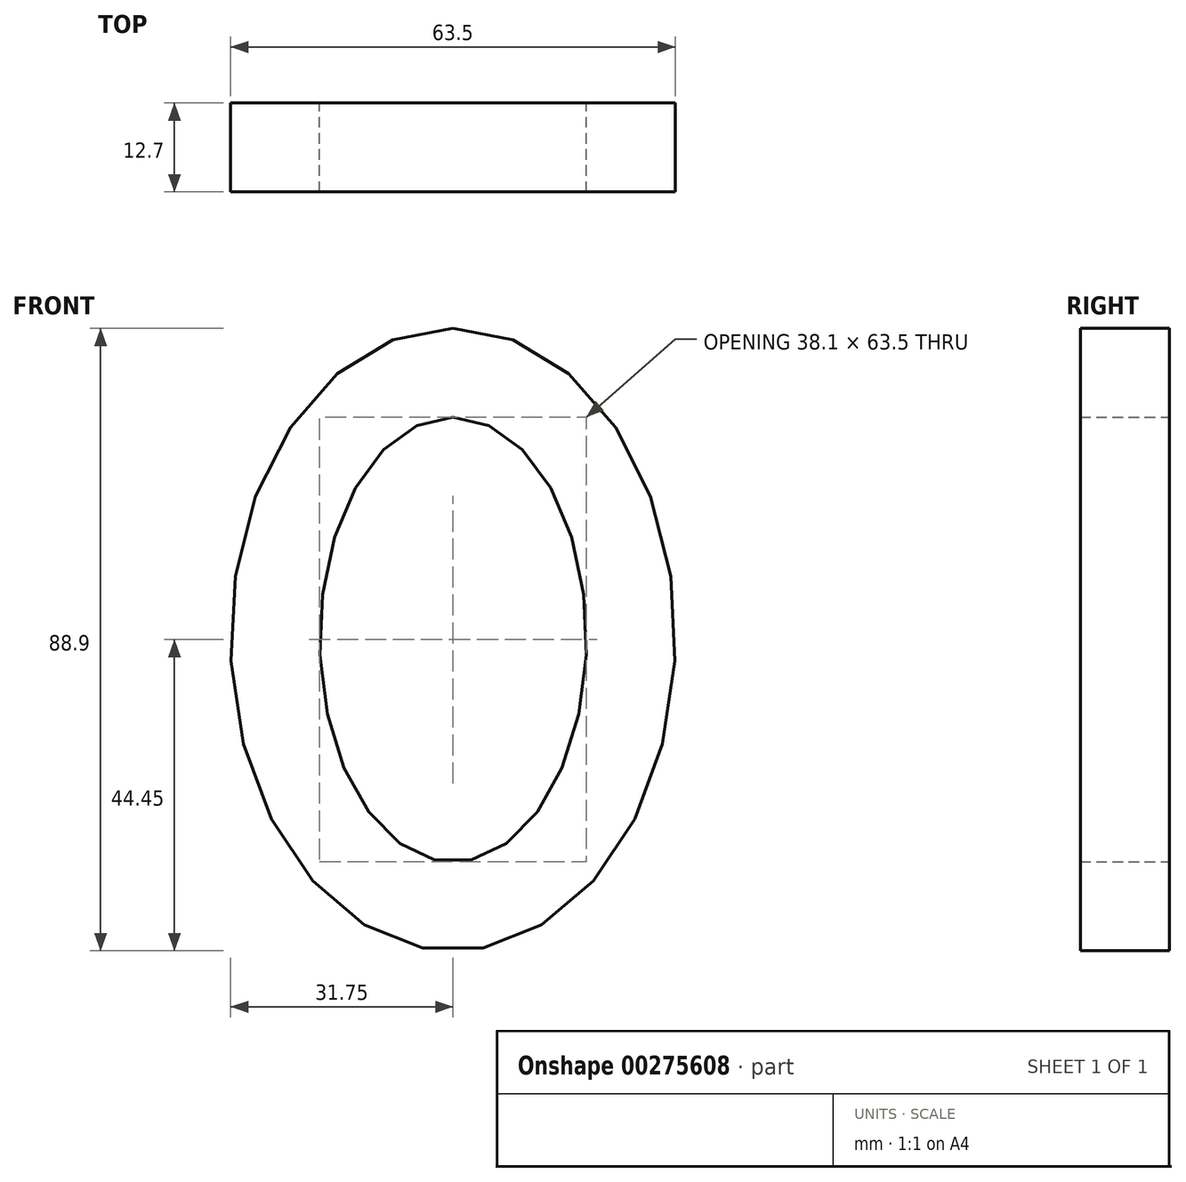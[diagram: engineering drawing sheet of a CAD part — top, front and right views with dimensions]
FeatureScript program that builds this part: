
annotation { "Feature Type Name" : "Feature", "Feature Type Description" : "" }
export const myFeature = defineFeature(function(context is Context, id is Id, definition is map)
    precondition{}
    {
        {
            var Q0;
            Q0=qCreatedBy(makeId("Front.planeOp"),FACE);
            var sketch = newSketch(context, id + "F0", { "sketchPlane" : qUnion([Q0])});
            skEllipse(sketch, "E0", {"center": v(0, 0) * mm, "majorRadius": 44.45 * mm, "minorRadius": 31.75 * mm, "majorAxis": v(0, 1)});
            skEllipse(sketch, "E1", {"center": v(0, 0) * mm, "majorRadius": 31.75 * mm, "minorRadius": 19.05 * mm, "majorAxis": v(0, 1)});
            skSolve(sketch);
        }
        {
            var Q0;
            Q0=makeQuery(id+"F0.imprint","IMPRINT",FACE,{"disambiguationData":[TD([[makeQuery(id+"F0.imprint","IMPRINT",EDGE,{"derivedFrom":sQuery(id+"F0.wireOp",EDGE,"E0")}),1.0]])]});
            extrude(context, id + "F1", {"entities" : qUnion([Q0]), "depth" : 12.7 * mm});
        }
    });
